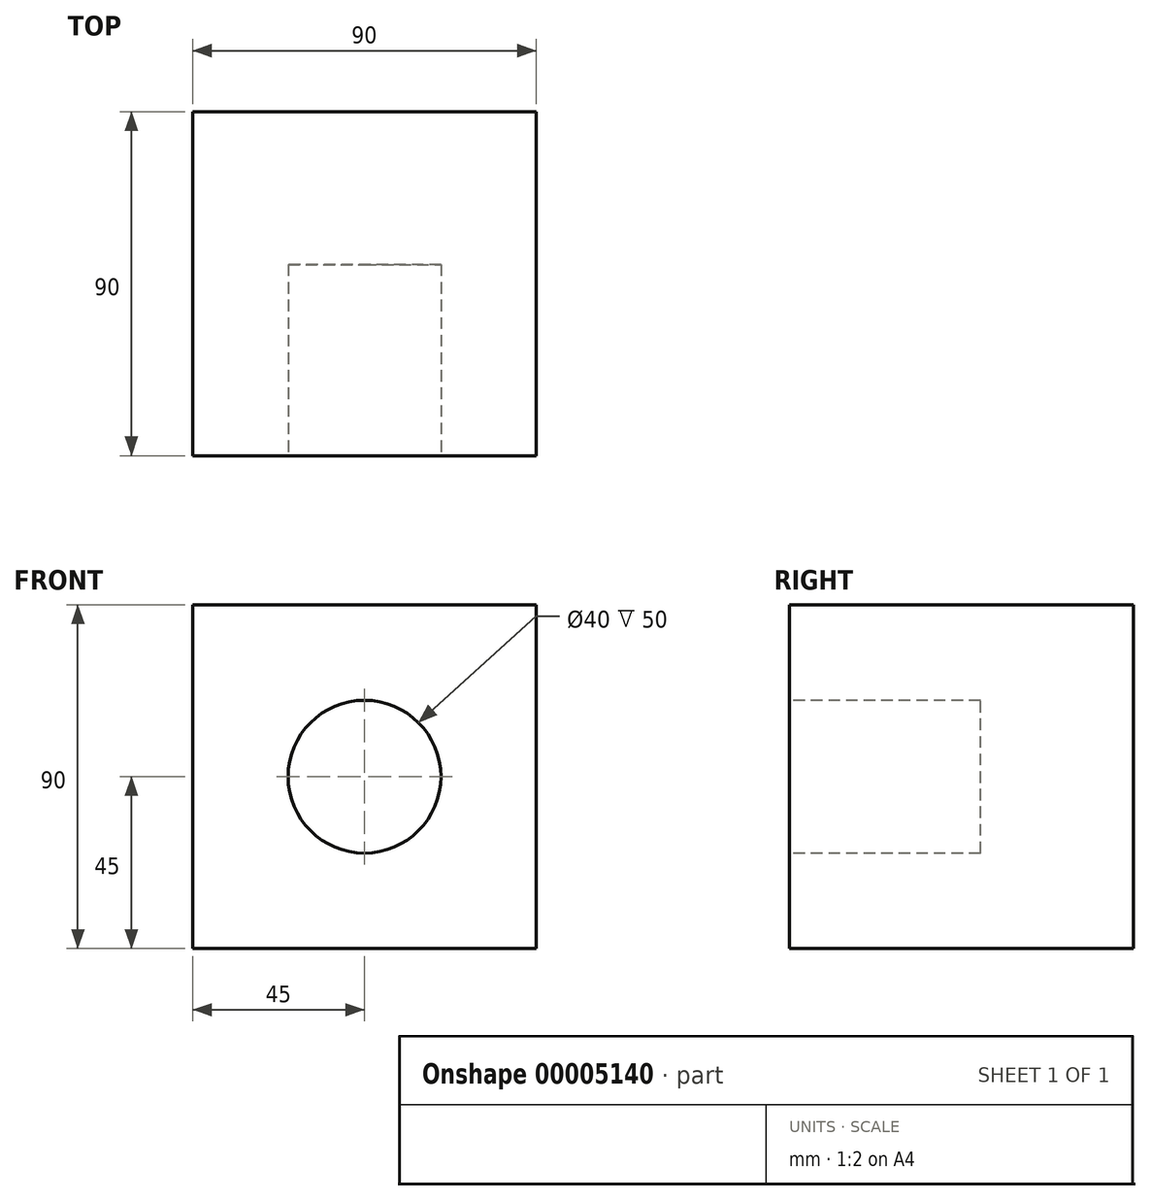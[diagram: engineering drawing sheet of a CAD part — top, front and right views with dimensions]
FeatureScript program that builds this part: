
annotation { "Feature Type Name" : "Feature", "Feature Type Description" : "" }
export const myFeature = defineFeature(function(context is Context, id is Id, definition is map)
    precondition{}
    {
        {
            var Q0;
            Q0=qCreatedBy(makeId("Front.planeOp"),FACE);
            var sketch = newSketch(context, id + "F0", { "sketchPlane" : qUnion([Q0])});
            skLineSegment(sketch, "E0.rect.bottom", {"start": v(-45, 45) * mm, "end": v(45, 45) * mm});
            skLineSegment(sketch, "E0.rect.top", {"start": v(-45, -45) * mm, "end": v(45, -45) * mm});
            skLineSegment(sketch, "E0.rect.left", {"start": v(-45, 45) * mm, "end": v(-45, -45) * mm});
            skLineSegment(sketch, "E0.rect.right", {"start": v(45, 45) * mm, "end": v(45, -45) * mm});
            skPoint(sketch, "E0.rect.middle", {"position": v(0, 0) * mm});
            skSolve(sketch);
        }
        {
            var Q0;
            Q0=makeQuery(id+"F0.imprint","IMPRINT",FACE,{"disambiguationData":[TD([[makeQuery(id+"F0.imprint","IMPRINT",EDGE,{"derivedFrom":sQuery(id+"F0.wireOp",EDGE,"E0.rect.bottom")}),-1.0]])]});
            extrude(context, id + "F1", {"entities" : qUnion([Q0]), "depth" : 90 * mm});
        }
        {
            var Q0;
            Q0=makeQuery(id+"F1.opExtrude","CAP_FACE",FACE,{"disambiguationData":[OSD([sQuery(id+"F0.wireOp",EDGE,"E0.rect.bottom"),sQuery(id+"F0.wireOp",EDGE,"E0.rect.top"),sQuery(id+"F0.wireOp",EDGE,"E0.rect.left"),sQuery(id+"F0.wireOp",EDGE,"E0.rect.right")])],"isStart":false});
            var sketch = newSketch(context, id + "F2", { "sketchPlane" : qUnion([Q0])});
            skCircle(sketch, "E1", {"center": v(0, 0) * mm, "radius": 20 * mm});
            skSolve(sketch);
        }
        {
            var Q0;
            Q0=makeQuery(id+"F2.imprint","IMPRINT",FACE,{"disambiguationData":[TD([[makeQuery(id+"F2.imprint","IMPRINT",EDGE,{"derivedFrom":sQuery(id+"F2.wireOp",EDGE,"E1")}),1.0]])]});
            extrude(context, id + "F3", {"entities" : qUnion([Q0]), "operationType" : NewBodyOperationType.REMOVE, "oppositeDirection" : true, "depth" : 50 * mm});
        }
    });
